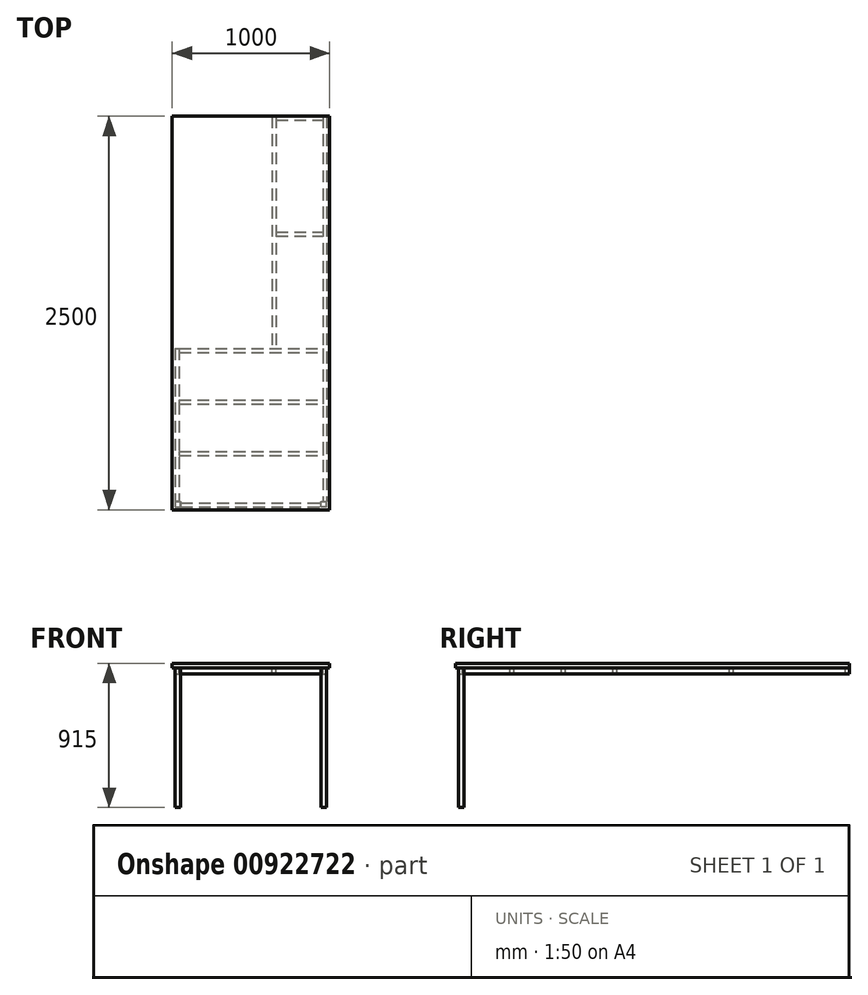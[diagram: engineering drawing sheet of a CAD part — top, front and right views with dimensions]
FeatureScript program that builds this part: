
annotation { "Feature Type Name" : "Feature", "Feature Type Description" : "" }
export const myFeature = defineFeature(function(context is Context, id is Id, definition is map)
    precondition{}
    {
        {
            var Q0;
            Q0=qCreatedBy(makeId("Top.planeOp"),FACE);
            var sketch = newSketch(context, id + "F0", { "sketchPlane" : qUnion([Q0])});
            skLineSegment(sketch, "E0.bottom", {"start": v(0, 0) * mm, "end": v(1000, 0) * mm});
            skLineSegment(sketch, "E0.top", {"start": v(0, -2500) * mm, "end": v(1000, -2500) * mm});
            skLineSegment(sketch, "E0.left", {"start": v(0, 0) * mm, "end": v(0, -2500) * mm});
            skLineSegment(sketch, "E0.right", {"start": v(1000, 0) * mm, "end": v(1000, -2500) * mm});
            skSolve(sketch);
        }
        {
            var Q0;
            Q0 = qSketchRegion(id + "F0", true);
            extrude(context, id + "F1", {"entities" : qUnion([Q0]), "depth" : 28 * mm, "offsetDistance" : 25 * mm});
        }
        {
            var Q0;
            Q0=qCreatedBy(makeId("Top.planeOp"),FACE);
            var sketch = newSketch(context, id + "F2", { "sketchPlane" : qUnion([Q0])});
            skLineSegment(sketch, "E1.bottom", {"start": v(635, -1475) * mm, "end": v(19, -1475) * mm, "construction": true});
            skLineSegment(sketch, "E1.top", {"start": v(635, 0) * mm, "end": v(19, 0) * mm, "construction": true});
            skLineSegment(sketch, "E1.left", {"start": v(635, -1475) * mm, "end": v(635, 0) * mm, "construction": true});
            skLineSegment(sketch, "E1.right", {"start": v(19, -1475) * mm, "end": v(19, 0) * mm, "construction": true});
            skLineSegment(sketch, "E2", {"start": v(19, -675) * mm, "end": v(635, -675) * mm, "construction": true});
            skLineSegment(sketch, "E3", {"start": v(19, -875) * mm, "end": v(635, -875) * mm, "construction": true});
            skLineSegment(sketch, "E4.bottom", {"start": v(635, 0) * mm, "end": v(660, 0) * mm});
            skLineSegment(sketch, "E4.top", {"start": v(635, -1475) * mm, "end": v(660, -1475) * mm});
            skLineSegment(sketch, "E4.left", {"start": v(635, 0) * mm, "end": v(635, -1475) * mm});
            skLineSegment(sketch, "E4.right", {"start": v(660, 0) * mm, "end": v(660, -1475) * mm});
            skLineSegment(sketch, "E5.bottom", {"start": v(956, 0) * mm, "end": v(981, 0) * mm});
            skLineSegment(sketch, "E5.top", {"start": v(956, -2446) * mm, "end": v(981, -2446) * mm});
            skLineSegment(sketch, "E5.left", {"start": v(956, 0) * mm, "end": v(956, -2446) * mm});
            skLineSegment(sketch, "E5.right", {"start": v(981, 0) * mm, "end": v(981, -2446) * mm});
            skLineSegment(sketch, "E6.bottom", {"start": v(19, -1475) * mm, "end": v(44, -1475) * mm});
            skLineSegment(sketch, "E7.bottom", {"start": v(44, -1475) * mm, "end": v(956, -1475) * mm});
            skLineSegment(sketch, "E7.top", {"start": v(44, -1500) * mm, "end": v(956, -1500) * mm});
            skLineSegment(sketch, "E7.left", {"start": v(44, -1475) * mm, "end": v(44, -1500) * mm});
            skLineSegment(sketch, "E7.right", {"start": v(956, -1475) * mm, "end": v(956, -1500) * mm});
            skLineSegment(sketch, "E8.bottom", {"start": v(660, 0) * mm, "end": v(956, 0) * mm});
            skLineSegment(sketch, "E8.top", {"start": v(660, -25) * mm, "end": v(956, -25) * mm});
            skLineSegment(sketch, "E8.left", {"start": v(660, 0) * mm, "end": v(660, -25) * mm});
            skLineSegment(sketch, "E8.right", {"start": v(956, 0) * mm, "end": v(956, -25) * mm});
            skLineSegment(sketch, "E9.bottom", {"start": v(660, -737.5) * mm, "end": v(956, -737.5) * mm});
            skLineSegment(sketch, "E9.top", {"start": v(660, -762.5) * mm, "end": v(956, -762.5) * mm});
            skLineSegment(sketch, "E9.left", {"start": v(660, -737.5) * mm, "end": v(660, -762.5) * mm});
            skLineSegment(sketch, "E9.right", {"start": v(956, -737.5) * mm, "end": v(956, -762.5) * mm});
            skLineSegment(sketch, "E10", {"start": v(808, -25) * mm, "end": v(808, -1475) * mm, "construction": true});
            skPoint(sketch, "E11", {"position": v(808, -750) * mm});
            skPoint(sketch, "E12", {"position": v(660, -750) * mm});
            skLineSegment(sketch, "E13.bottom", {"start": v(44, -1802) * mm, "end": v(956, -1802) * mm});
            skLineSegment(sketch, "E13.top", {"start": v(44, -1827) * mm, "end": v(956, -1827) * mm});
            skLineSegment(sketch, "E13.left", {"start": v(44, -1802) * mm, "end": v(44, -1827) * mm});
            skLineSegment(sketch, "E13.right", {"start": v(956, -1802) * mm, "end": v(956, -1827) * mm});
            skLineSegment(sketch, "E14.bottom", {"start": v(44, -2129) * mm, "end": v(956, -2129) * mm});
            skLineSegment(sketch, "E14.top", {"start": v(44, -2154) * mm, "end": v(956, -2154) * mm});
            skLineSegment(sketch, "E14.left", {"start": v(44, -2129) * mm, "end": v(44, -2154) * mm});
            skLineSegment(sketch, "E14.right", {"start": v(956, -2129) * mm, "end": v(956, -2154) * mm});
            skLineSegment(sketch, "E15", {"start": v(300.09, -1500) * mm, "end": v(300.09, -1802) * mm, "construction": true});
            skLineSegment(sketch, "E16", {"start": v(301.86, -1827) * mm, "end": v(301.86, -2129) * mm, "construction": true});
            skLineSegment(sketch, "E17", {"start": v(300, -2154) * mm, "end": v(300, -2456) * mm, "construction": true});
            skLineSegment(sketch, "E18.bottom", {"start": v(981, -2481) * mm, "end": v(946, -2481) * mm});
            skLineSegment(sketch, "E18.top", {"start": v(981, -2446) * mm, "end": v(946, -2446) * mm});
            skLineSegment(sketch, "E18.left", {"start": v(981, -2481) * mm, "end": v(981, -2446) * mm});
            skLineSegment(sketch, "E18.right", {"start": v(946, -2481) * mm, "end": v(946, -2446) * mm});
            skLineSegment(sketch, "E19.bottom", {"start": v(54, -2481) * mm, "end": v(19, -2481) * mm});
            skLineSegment(sketch, "E19.top", {"start": v(54, -2446) * mm, "end": v(19, -2446) * mm});
            skLineSegment(sketch, "E19.left", {"start": v(54, -2481) * mm, "end": v(54, -2446) * mm});
            skLineSegment(sketch, "E19.right", {"start": v(19, -2481) * mm, "end": v(19, -2446) * mm});
            skLineSegment(sketch, "E20.top", {"start": v(19, -2446) * mm, "end": v(44, -2446) * mm});
            skLineSegment(sketch, "E20.left", {"start": v(19, -1475) * mm, "end": v(19, -2446) * mm});
            skLineSegment(sketch, "E20.right", {"start": v(44, -1475) * mm, "end": v(44, -2446) * mm});
            skLineSegment(sketch, "E21.bottom", {"start": v(54, -2481) * mm, "end": v(946, -2481) * mm});
            skLineSegment(sketch, "E21.top", {"start": v(54, -2456) * mm, "end": v(946, -2456) * mm});
            skLineSegment(sketch, "E21.left", {"start": v(54, -2481) * mm, "end": v(54, -2456) * mm});
            skLineSegment(sketch, "E21.right", {"start": v(946, -2481) * mm, "end": v(946, -2456) * mm});
            skSolve(sketch);
        }
        {
            var Q0;
            Q0=makeQuery(id+"F2.imprint","IMPRINT",FACE,{"disambiguationData":[TD([[makeQuery(id+"F2.imprint","IMPRINT",EDGE,{"derivedFrom":sQuery(id+"F2.wireOp",EDGE,"E4.bottom")}),-1.0]])]});
            extrude(context, id + "F3", {"entities" : qUnion([Q0]), "oppositeDirection" : true, "depth" : 40 * mm, "offsetDistance" : 25 * mm});
        }
        {
            var Q0;
            {var subQ3=sQuery(id+"F2.wireOp",EDGE,"E5.bottom");Q0=makeQuery(id+"F2.imprint","IMPRINT",FACE,{"disambiguationData":[TD([[makeQuery(id+"F2.imprint","IMPRINT",EDGE,{"derivedFrom":subQ3}),-1.0]])]});}
            extrude(context, id + "F4", {"entities" : qUnion([Q0]), "oppositeDirection" : true, "depth" : 40 * mm, "offsetDistance" : 25 * mm});
        }
        {
            var Q0;
            Q0=makeQuery(id+"F2.imprint","IMPRINT",FACE,{"disambiguationData":[TD([[makeQuery(id+"F2.imprint","IMPRINT",EDGE,{"derivedFrom":sQuery(id+"F2.wireOp",EDGE,"E7.top")}),1.0]])]});
            extrude(context, id + "F5", {"entities" : qUnion([Q0]), "oppositeDirection" : true, "depth" : 40 * mm, "offsetDistance" : 25 * mm});
        }
        {
            var Q0;
            Q0=makeQuery(id+"F2.imprint","IMPRINT",FACE,{"disambiguationData":[TD([[makeQuery(id+"F2.imprint","IMPRINT",EDGE,{"derivedFrom":sQuery(id+"F2.wireOp",EDGE,"E8.bottom")}),-1.0]])]});
            extrude(context, id + "F6", {"entities" : qUnion([Q0]), "oppositeDirection" : true, "depth" : 40 * mm, "offsetDistance" : 25 * mm});
        }
        {
            var Q0;
            Q0=makeQuery(id+"F2.imprint","IMPRINT",FACE,{"disambiguationData":[TD([[makeQuery(id+"F2.imprint","IMPRINT",EDGE,{"derivedFrom":sQuery(id+"F2.wireOp",EDGE,"E9.bottom")}),-1.0]])]});
            extrude(context, id + "F7", {"entities" : qUnion([Q0]), "oppositeDirection" : true, "depth" : 40 * mm, "offsetDistance" : 25 * mm});
        }
        {
            var Q0;
            Q0=makeQuery(id+"F2.imprint","IMPRINT",FACE,{"disambiguationData":[TD([[makeQuery(id+"F2.imprint","IMPRINT",EDGE,{"derivedFrom":sQuery(id+"F2.wireOp",EDGE,"E13.bottom")}),-1.0]])]});
            extrude(context, id + "F8", {"entities" : qUnion([Q0]), "oppositeDirection" : true, "depth" : 40 * mm, "offsetDistance" : 25 * mm});
        }
        {
            var Q0;
            Q0=makeQuery(id+"F2.imprint","IMPRINT",FACE,{"disambiguationData":[TD([[makeQuery(id+"F2.imprint","IMPRINT",EDGE,{"derivedFrom":sQuery(id+"F2.wireOp",EDGE,"E14.bottom")}),-1.0]])]});
            extrude(context, id + "F9", {"entities" : qUnion([Q0]), "oppositeDirection" : true, "depth" : 40 * mm, "offsetDistance" : 25 * mm});
        }
        {
            var Q0;
            {var subQ1=sQuery(id+"F2.wireOp",EDGE,"E6.bottom");Q0=makeQuery(id+"F2.imprint","IMPRINT",FACE,{"disambiguationData":[TD([[makeQuery(id+"F2.imprint","IMPRINT",EDGE,{"derivedFrom":subQ1}),-1.0]])]});}
            extrude(context, id + "F10", {"entities" : qUnion([Q0]), "oppositeDirection" : true, "depth" : 40 * mm, "offsetDistance" : 25 * mm});
        }
        {
            var Q0;
            Q0=makeQuery(id+"F2.imprint","IMPRINT",FACE,{"disambiguationData":[TD([[makeQuery(id+"F2.imprint","IMPRINT",EDGE,{"derivedFrom":sQuery(id+"F2.wireOp",EDGE,"E18.bottom")}),-1.0]])]});
            extrude(context, id + "F11", {"entities" : qUnion([Q0]), "oppositeDirection" : true, "depth" : 887 * mm, "offsetDistance" : 25 * mm});
        }
        {
            var Q0;
            Q0=makeQuery(id+"F2.imprint","IMPRINT",FACE,{"disambiguationData":[TD([[makeQuery(id+"F2.imprint","IMPRINT",EDGE,{"derivedFrom":sQuery(id+"F2.wireOp",EDGE,"E19.bottom")}),-1.0]])]});
            var Q1;
            Q1=makeQuery(id+"F11.opExtrude","CAP_FACE",FACE,{"disambiguationData":[OSD([sQuery(id+"F2.wireOp",EDGE,"E18.bottom"),sQuery(id+"F2.wireOp",EDGE,"E18.top"),sQuery(id+"F2.wireOp",EDGE,"E18.left"),sQuery(id+"F2.wireOp",EDGE,"E18.right"),sQuery(id+"F2.wireOp",EDGE,"E21.right")])],"isStart":false});
            extrude(context, id + "F12", {"entities" : qUnion([Q0]), "endBound" : BoundingType.UP_TO_SURFACE, "oppositeDirection" : true, "depth" : 900 * mm, "endBoundEntityFace" : qUnion([Q1]), "offsetDistance" : 25 * mm});
        }
        {
            var Q0;
            Q0=makeQuery(id+"F2.imprint","IMPRINT",FACE,{"disambiguationData":[TD([[makeQuery(id+"F2.imprint","IMPRINT",EDGE,{"derivedFrom":sQuery(id+"F2.wireOp",EDGE,"E21.bottom")}),1.0]])]});
            extrude(context, id + "F13", {"entities" : qUnion([Q0]), "oppositeDirection" : true, "depth" : 40 * mm, "offsetDistance" : 25 * mm});
        }
    });
